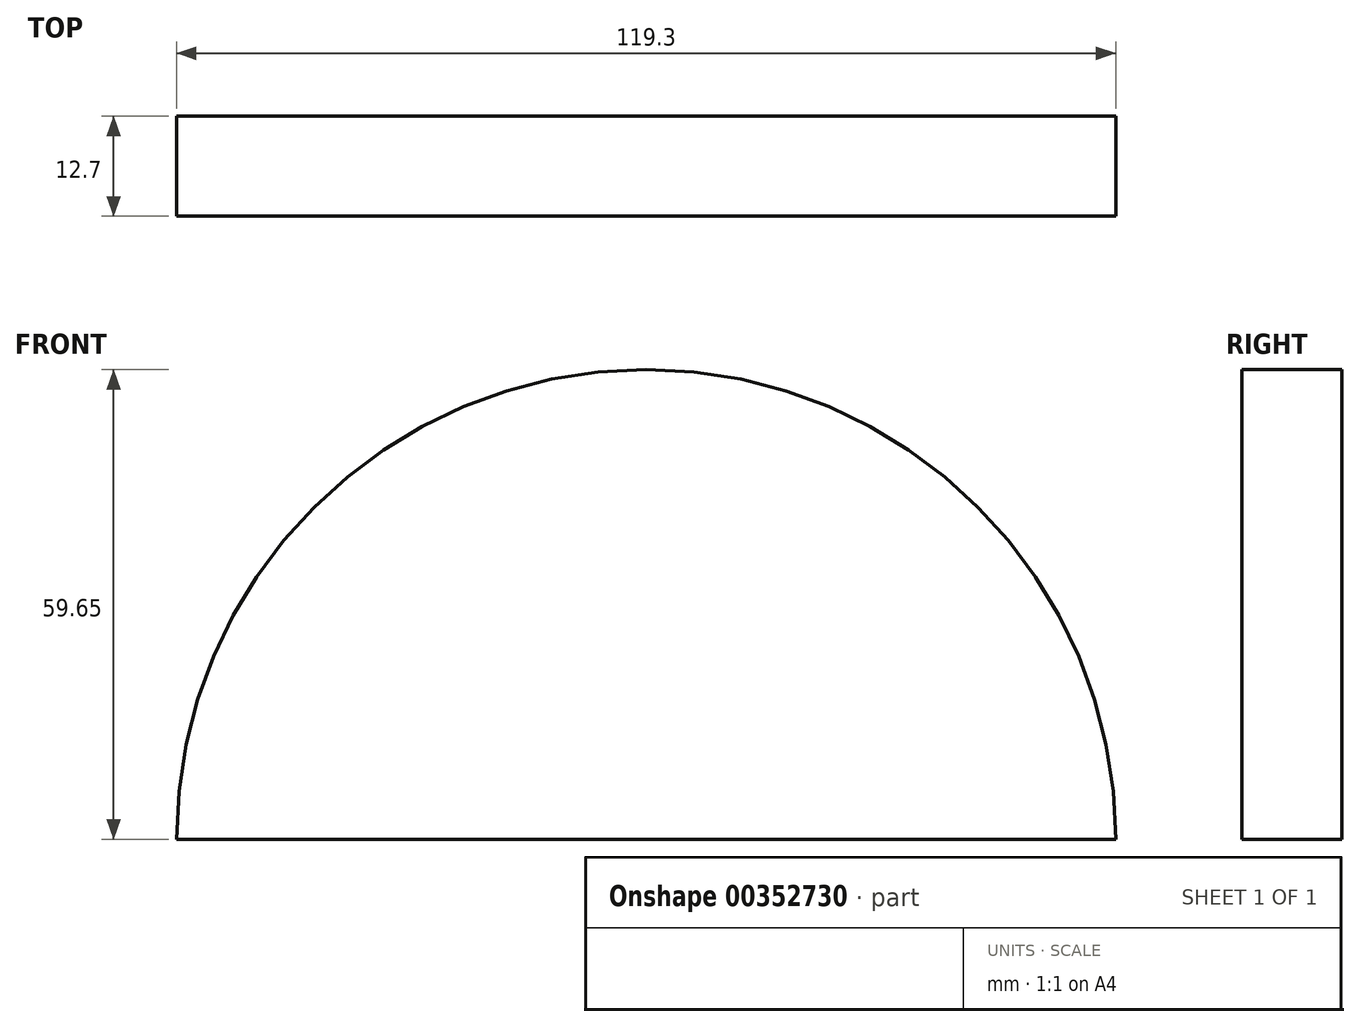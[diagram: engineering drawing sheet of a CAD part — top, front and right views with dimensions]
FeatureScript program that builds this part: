
annotation { "Feature Type Name" : "Feature", "Feature Type Description" : "" }
export const myFeature = defineFeature(function(context is Context, id is Id, definition is map)
    precondition{}
    {
        {
            var Q0;
            Q0=qCreatedBy(makeId("Front.planeOp"),FACE);
            var sketch = newSketch(context, id + "F0", { "sketchPlane" : qUnion([Q0])});
            skArc(sketch, "E0", {"start": v(59.65, 0) * mm, "mid": v(0, 59.65) * mm, "end": v(-59.65, 0) * mm});
            skLineSegment(sketch, "E1.bottom", {"start": v(-59.65, 0) * mm, "end": v(59.76, 0) * mm});
            skSolve(sketch);
        }
        {
            var Q0;
            Q0=qSketchRegion(id+"F0",true);
            extrude(context, id + "F1", {"entities" : qUnion([Q0]), "depth" : 12.7 * mm});
        }
    });
